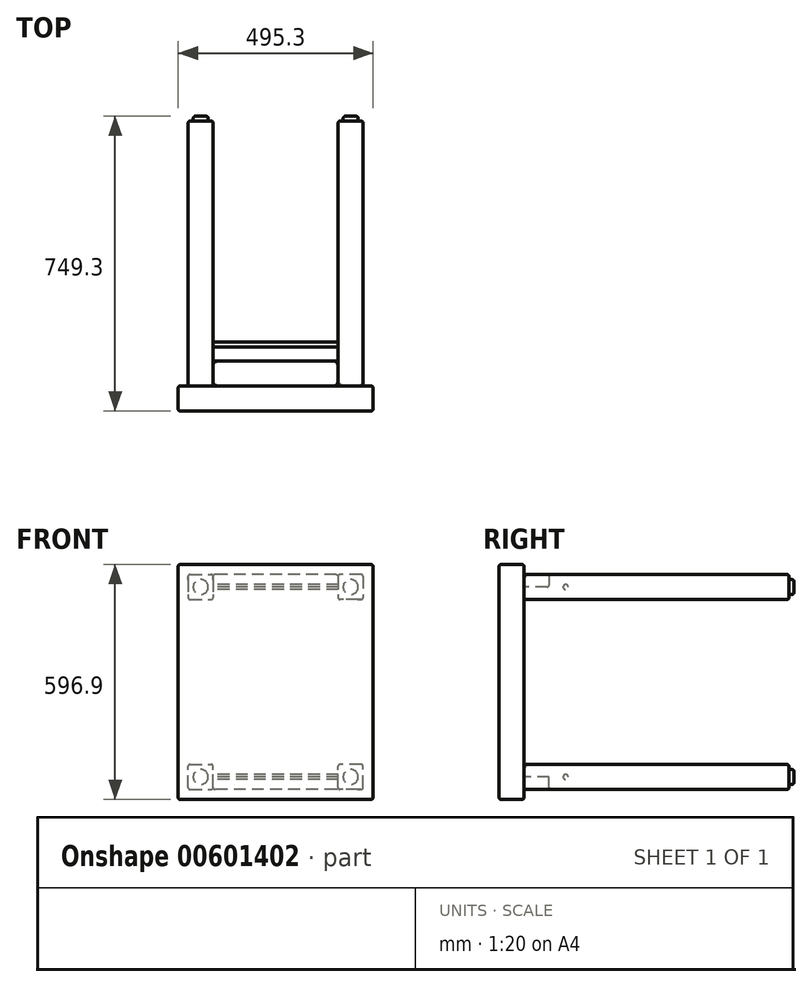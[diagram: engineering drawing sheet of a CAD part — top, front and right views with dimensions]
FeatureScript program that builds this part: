
annotation { "Feature Type Name" : "Feature", "Feature Type Description" : "" }
export const myFeature = defineFeature(function(context is Context, id is Id, definition is map)
    precondition{}
    {
        {
            var Q0;
            Q0=qCreatedBy(makeId("Front.planeOp"),FACE);
            var sketch = newSketch(context, id + "F0", { "sketchPlane" : qUnion([Q0])});
            skLineSegment(sketch, "E0.bottom", {"start": v(-247.65, 298.45) * mm, "end": v(247.65, 298.45) * mm});
            skLineSegment(sketch, "E0.top", {"start": v(-247.65, -298.45) * mm, "end": v(247.65, -298.45) * mm});
            skLineSegment(sketch, "E0.left", {"start": v(-247.65, 298.45) * mm, "end": v(-247.65, -298.45) * mm});
            skLineSegment(sketch, "E0.right", {"start": v(247.65, 298.45) * mm, "end": v(247.65, -298.45) * mm});
            skPoint(sketch, "E0.middle", {"position": v(0, 0) * mm});
            skSolve(sketch);
        }
        {
            var Q0;
            Q0 = qSketchRegion(id + "F0", true);
            extrude(context, id + "F1", {"entities" : qUnion([Q0]), "endBound" : BoundingType.SYMMETRIC, "depth" : 63.5 * mm, "offsetDistance" : 25.4 * mm});
        }
        {
            var Q0;
            Q0=makeQuery(id+"F1.opExtrude","CAP_FACE",FACE,{"disambiguationData":[OSD([sQuery(id+"F0.wireOp",EDGE,"E0.bottom"),sQuery(id+"F0.wireOp",EDGE,"E0.top"),sQuery(id+"F0.wireOp",EDGE,"E0.left"),sQuery(id+"F0.wireOp",EDGE,"E0.right")])],"isStart":true});
            var sketch = newSketch(context, id + "F2", { "sketchPlane" : qUnion([Q0])});
            skLineSegment(sketch, "E1.bottom", {"start": v(-222.25, 273.05) * mm, "end": v(222.25, 273.05) * mm, "construction": true});
            skLineSegment(sketch, "E1.top", {"start": v(-222.25, -273.05) * mm, "end": v(222.25, -273.05) * mm, "construction": true});
            skLineSegment(sketch, "E1.left", {"start": v(-222.25, 273.05) * mm, "end": v(-222.25, -273.05) * mm, "construction": true});
            skLineSegment(sketch, "E1.right", {"start": v(222.25, 273.05) * mm, "end": v(222.25, -273.05) * mm, "construction": true});
            skPoint(sketch, "E1.middle", {"position": v(0, 0) * mm});
            skLineSegment(sketch, "E2.bottom", {"start": v(-222.25, 273.05) * mm, "end": v(-158.75, 273.05) * mm});
            skLineSegment(sketch, "E2.top", {"start": v(-222.25, 209.55) * mm, "end": v(-158.75, 209.55) * mm});
            skLineSegment(sketch, "E2.left", {"start": v(-222.25, 273.05) * mm, "end": v(-222.25, 209.55) * mm});
            skLineSegment(sketch, "E2.right", {"start": v(-158.75, 273.05) * mm, "end": v(-158.75, 209.55) * mm});
            skLineSegment(sketch, "E3.bottom", {"start": v(222.25, 273.05) * mm, "end": v(158.75, 273.05) * mm});
            skLineSegment(sketch, "E3.top", {"start": v(222.25, 209.55) * mm, "end": v(158.75, 209.55) * mm});
            skLineSegment(sketch, "E3.left", {"start": v(222.25, 273.05) * mm, "end": v(222.25, 209.55) * mm});
            skLineSegment(sketch, "E3.right", {"start": v(158.75, 273.05) * mm, "end": v(158.75, 209.55) * mm});
            skLineSegment(sketch, "E4.bottom", {"start": v(222.25, -273.05) * mm, "end": v(158.75, -273.05) * mm});
            skLineSegment(sketch, "E4.top", {"start": v(222.25, -209.55) * mm, "end": v(158.75, -209.55) * mm});
            skLineSegment(sketch, "E4.left", {"start": v(222.25, -273.05) * mm, "end": v(222.25, -209.55) * mm});
            skLineSegment(sketch, "E4.right", {"start": v(158.75, -273.05) * mm, "end": v(158.75, -209.55) * mm});
            skLineSegment(sketch, "E5.bottom", {"start": v(-222.25, -273.05) * mm, "end": v(-158.75, -273.05) * mm});
            skLineSegment(sketch, "E5.top", {"start": v(-222.25, -209.55) * mm, "end": v(-158.75, -209.55) * mm});
            skLineSegment(sketch, "E5.left", {"start": v(-222.25, -273.05) * mm, "end": v(-222.25, -209.55) * mm});
            skLineSegment(sketch, "E5.right", {"start": v(-158.75, -273.05) * mm, "end": v(-158.75, -209.55) * mm});
            skLineSegment(sketch, "E6.bottom", {"start": v(-222.25, 209.55) * mm, "end": v(-190.5, 209.55) * mm});
            skLineSegment(sketch, "E6.top", {"start": v(-222.25, -209.55) * mm, "end": v(-190.5, -209.55) * mm});
            skLineSegment(sketch, "E6.left", {"start": v(-222.25, 209.55) * mm, "end": v(-222.25, -209.55) * mm});
            skLineSegment(sketch, "E6.right", {"start": v(-190.5, 209.55) * mm, "end": v(-190.5, -209.55) * mm});
            skLineSegment(sketch, "E7.bottom", {"start": v(222.25, -209.55) * mm, "end": v(190.5, -209.55) * mm});
            skLineSegment(sketch, "E7.top", {"start": v(222.25, 209.55) * mm, "end": v(190.5, 209.55) * mm});
            skLineSegment(sketch, "E7.left", {"start": v(222.25, -209.55) * mm, "end": v(222.25, 209.55) * mm});
            skLineSegment(sketch, "E7.right", {"start": v(190.5, -209.55) * mm, "end": v(190.5, 209.55) * mm});
            skLineSegment(sketch, "E8.bottom", {"start": v(-158.75, 273.05) * mm, "end": v(158.75, 273.05) * mm});
            skLineSegment(sketch, "E8.top", {"start": v(-158.75, 241.3) * mm, "end": v(158.75, 241.3) * mm});
            skLineSegment(sketch, "E8.left", {"start": v(-158.75, 273.05) * mm, "end": v(-158.75, 241.3) * mm});
            skLineSegment(sketch, "E8.right", {"start": v(158.75, 273.05) * mm, "end": v(158.75, 241.3) * mm});
            skLineSegment(sketch, "E9.bottom", {"start": v(-158.75, -273.05) * mm, "end": v(158.75, -273.05) * mm});
            skLineSegment(sketch, "E9.top", {"start": v(-158.75, -241.3) * mm, "end": v(158.75, -241.3) * mm});
            skLineSegment(sketch, "E9.left", {"start": v(-158.75, -273.05) * mm, "end": v(-158.75, -241.3) * mm});
            skLineSegment(sketch, "E9.right", {"start": v(158.75, -273.05) * mm, "end": v(158.75, -241.3) * mm});
            skSolve(sketch);
        }
        {
            var Q0;
            Q0=makeQuery(id+"F2.imprint","IMPRINT",FACE,{"disambiguationData":[TD([[makeQuery(id+"F2.imprint","IMPRINT",EDGE,{"derivedFrom":sQuery(id+"F2.wireOp",EDGE,"E3.bottom")}),1.0]])]});
            var Q1;
            Q1=makeQuery(id+"F2.imprint","IMPRINT",FACE,{"disambiguationData":[TD([[makeQuery(id+"F2.imprint","IMPRINT",EDGE,{"derivedFrom":sQuery(id+"F2.wireOp",EDGE,"E4.bottom")}),-1.0]])]});
            var Q2;
            Q2=makeQuery(id+"F2.imprint","IMPRINT",FACE,{"disambiguationData":[TD([[makeQuery(id+"F2.imprint","IMPRINT",EDGE,{"derivedFrom":sQuery(id+"F2.wireOp",EDGE,"E5.bottom")}),1.0]])]});
            var Q3;
            Q3=makeQuery(id+"F2.imprint","IMPRINT",FACE,{"disambiguationData":[TD([[makeQuery(id+"F2.imprint","IMPRINT",EDGE,{"derivedFrom":sQuery(id+"F2.wireOp",EDGE,"E2.bottom")}),-1.0]])]});
            extrude(context, id + "F3", {"entities" : qUnion([Q0, Q1, Q2, Q3]), "operationType" : NewBodyOperationType.ADD, "depth" : 673.1 * mm, "offsetDistance" : 25.4 * mm});
        }
        {
            var Q0;
            Q0=makeQuery(id+"F2.imprint","IMPRINT",FACE,{"disambiguationData":[TD([[makeQuery(id+"F2.imprint","IMPRINT",EDGE,{"derivedFrom":sQuery(id+"F2.wireOp",EDGE,"E8.bottom")}),-1.0]])]});
            var Q1;
            Q1=makeQuery(id+"F2.imprint","IMPRINT",FACE,{"disambiguationData":[TD([[makeQuery(id+"F2.imprint","IMPRINT",EDGE,{"derivedFrom":sQuery(id+"F2.wireOp",EDGE,"E7.bottom")}),-1.0]])]});
            var Q2;
            Q2=makeQuery(id+"F2.imprint","IMPRINT",FACE,{"disambiguationData":[TD([[makeQuery(id+"F2.imprint","IMPRINT",EDGE,{"derivedFrom":sQuery(id+"F2.wireOp",EDGE,"E9.bottom")}),1.0]])]});
            var Q3;
            Q3=makeQuery(id+"F2.imprint","IMPRINT",FACE,{"disambiguationData":[TD([[makeQuery(id+"F2.imprint","IMPRINT",EDGE,{"derivedFrom":sQuery(id+"F2.wireOp",EDGE,"E6.bottom")}),-1.0]])]});
            extrude(context, id + "F4", {"entities" : qUnion([Q0, Q1, Q2, Q3]), "depth" : 63.5 * mm, "offsetDistance" : 25.4 * mm});
        }
        {
            var Q0;
            Q0=makeQuery(id+"F3.opExtrude","CAP_FACE",FACE,{"disambiguationData":[OSD([sQuery(id+"F2.wireOp",EDGE,"E3.bottom"),sQuery(id+"F2.wireOp",EDGE,"E3.top"),sQuery(id+"F2.wireOp",EDGE,"E3.left"),sQuery(id+"F2.wireOp",EDGE,"E3.right"),sQuery(id+"F2.wireOp",EDGE,"E7.top"),sQuery(id+"F2.wireOp",EDGE,"E8.right")])],"isStart":false});
            var sketch = newSketch(context, id + "F5", { "sketchPlane" : qUnion([Q0])});
            skCircle(sketch, "E10", {"center": v(-190.5, 241.3) * mm, "radius": 19.05 * mm});
            skPoint(sketch, "E10.centerSnap0", {"position": v(-190.5, 209.55) * mm});
            skPoint(sketch, "E10.centerSnap1", {"position": v(-222.25, 241.3) * mm});
            skCircle(sketch, "E11", {"center": v(-190.5, -241.3) * mm, "radius": 19.05 * mm});
            skPoint(sketch, "E11.centerSnap0", {"position": v(-222.25, -241.3) * mm});
            skPoint(sketch, "E11.centerSnap1", {"position": v(-190.5, -273.05) * mm});
            skCircle(sketch, "E12", {"center": v(190.5, -241.3) * mm, "radius": 19.05 * mm});
            skPoint(sketch, "E12.centerSnap0", {"position": v(190.5, -273.05) * mm});
            skPoint(sketch, "E12.centerSnap1", {"position": v(222.25, -241.3) * mm});
            skCircle(sketch, "E13", {"center": v(190.5, 241.3) * mm, "radius": 19.05 * mm});
            skPoint(sketch, "E13.centerSnap0", {"position": v(158.75, 241.3) * mm});
            skPoint(sketch, "E13.centerSnap1", {"position": v(190.5, 209.55) * mm});
            skSolve(sketch);
        }
        {
            var Q0;
            Q0=makeQuery(id+"F5.imprint","IMPRINT",FACE,{"disambiguationData":[TD([[makeQuery(id+"F5.imprint","IMPRINT",EDGE,{"derivedFrom":sQuery(id+"F5.wireOp",EDGE,"E10")}),1.0]])]});
            var Q1;
            Q1=makeQuery(id+"F5.imprint","IMPRINT",FACE,{"disambiguationData":[TD([[makeQuery(id+"F5.imprint","IMPRINT",EDGE,{"derivedFrom":sQuery(id+"F5.wireOp",EDGE,"E11")}),1.0]])]});
            var Q2;
            Q2=makeQuery(id+"F5.imprint","IMPRINT",FACE,{"disambiguationData":[TD([[makeQuery(id+"F5.imprint","IMPRINT",EDGE,{"derivedFrom":sQuery(id+"F5.wireOp",EDGE,"E12")}),1.0]])]});
            var Q3;
            Q3=makeQuery(id+"F5.imprint","IMPRINT",FACE,{"disambiguationData":[TD([[makeQuery(id+"F5.imprint","IMPRINT",EDGE,{"derivedFrom":sQuery(id+"F5.wireOp",EDGE,"E13")}),1.0]])]});
            extrude(context, id + "F6", {"entities" : qUnion([Q0, Q1, Q2, Q3]), "depth" : 12.7 * mm, "offsetDistance" : 25.4 * mm});
        }
        {
            var Q0;
            Q0=makeQuery(id+"F6.opExtrude","CAP_FACE",FACE,{"disambiguationData":[OSD([sQuery(id+"F5.wireOp",EDGE,"E10")])],"isStart":false});
            var Q1;
            Q1=makeQuery(id+"F6.opExtrude","CAP_FACE",FACE,{"disambiguationData":[OSD([sQuery(id+"F5.wireOp",EDGE,"E13")])],"isStart":false});
            var Q2;
            Q2=makeQuery(id+"F6.opExtrude","CAP_FACE",FACE,{"disambiguationData":[OSD([sQuery(id+"F5.wireOp",EDGE,"E12")])],"isStart":false});
            var Q3;
            Q3=makeQuery(id+"F6.opExtrude","CAP_FACE",FACE,{"disambiguationData":[OSD([sQuery(id+"F5.wireOp",EDGE,"E11")])],"isStart":false});
            fillet(context, id + "F7", {"entities" : qUnion([Q0, Q1, Q2, Q3]), "radius" : 6.35 * mm, "tangentPropagation" : true, "allowEdgeOverflow" : false});
        }
        {
            var Q0;
            Q0=makeQuery(id+"F4.opExtrude","CAP_EDGE",EDGE,{"disambiguationData":[OSD([sQuery(id+"F2.wireOp",EDGE,"E8.bottom")])],"isStart":false});
            var Q1;
            Q1=makeQuery(id+"F4.opExtrude","CAP_EDGE",EDGE,{"disambiguationData":[OSD([sQuery(id+"F2.wireOp",EDGE,"E8.top")])],"isStart":false});
            var Q2;
            Q2=makeQuery(id+"F4.opExtrude","SWEPT_FACE",FACE,{"disambiguationData":[OSD([sQuery(id+"F2.wireOp",EDGE,"E8.bottom")])]});
            var Q3;
            Q3=makeQuery(id+"F3.opExtrude","SWEPT_FACE",FACE,{"disambiguationData":[OSD([sQuery(id+"F2.wireOp",EDGE,"E3.bottom")])]});
            var Q4;
            Q4=makeQuery(id+"F3.opExtrude","SWEPT_FACE",FACE,{"disambiguationData":[OSD([sQuery(id+"F2.wireOp",EDGE,"E4.top"),sQuery(id+"F2.wireOp",EDGE,"E7.bottom")])]});
            var Q5;
            Q5=makeQuery(id+"F3.opExtrude","SWEPT_FACE",FACE,{"disambiguationData":[OSD([sQuery(id+"F2.wireOp",EDGE,"E5.top"),sQuery(id+"F2.wireOp",EDGE,"E6.top")])]});
            var Q6;
            Q6=makeQuery(id+"F3.opExtrude","SWEPT_FACE",FACE,{"disambiguationData":[OSD([sQuery(id+"F2.wireOp",EDGE,"E2.bottom")])]});
            var Q7;
            Q7=makeQuery(id+"F3.opExtrude","SWEPT_EDGE",EDGE,{"disambiguationData":[OSD([sQuery(id+"F2.wireOp",EDGE,"E3.left"),sQuery(id+"F2.wireOp",EDGE,"E7.top"),sQuery(id+"F2.wireOp",EDGE,"E7.left")])]});
            var Q8;
            Q8=makeQuery(id+"F3.opExtrude","SWEPT_EDGE",EDGE,{"disambiguationData":[OSD([sQuery(id+"F2.wireOp",EDGE,"E4.bottom"),sQuery(id+"F2.wireOp",EDGE,"E4.left")])]});
            var Q9;
            Q9=makeQuery(id+"F1.opExtrude","CAP_EDGE",EDGE,{"disambiguationData":[OSD([sQuery(id+"F0.wireOp",EDGE,"E0.left")])],"isStart":true});
            var Q10;
            Q10=makeQuery(id+"F4.opExtrude","SWEPT_FACE",FACE,{"disambiguationData":[OSD([sQuery(id+"F2.wireOp",EDGE,"E7.left")])]});
            var Q11;
            Q11=makeQuery(id+"F1.opExtrude","SWEPT_FACE",FACE,{"disambiguationData":[OSD([sQuery(id+"F0.wireOp",EDGE,"E0.left")])]});
            var Q12;
            Q12=makeQuery(id+"F1.opExtrude","CAP_FACE",FACE,{"disambiguationData":[OSD([sQuery(id+"F0.wireOp",EDGE,"E0.bottom"),sQuery(id+"F0.wireOp",EDGE,"E0.top"),sQuery(id+"F0.wireOp",EDGE,"E0.left"),sQuery(id+"F0.wireOp",EDGE,"E0.right")])],"isStart":false});
            var Q13;
            Q13=makeQuery(id+"F3.opExtrude","SWEPT_FACE",FACE,{"disambiguationData":[OSD([sQuery(id+"F2.wireOp",EDGE,"E2.left")])]});
            var Q14;
            Q14=makeQuery(id+"F3.opExtrude","SWEPT_FACE",FACE,{"disambiguationData":[OSD([sQuery(id+"F2.wireOp",EDGE,"E5.left")])]});
            var Q15;
            Q15=makeQuery(id+"F3.opExtrude","SWEPT_EDGE",EDGE,{"disambiguationData":[OSD([sQuery(id+"F2.wireOp",EDGE,"E4.bottom"),sQuery(id+"F2.wireOp",EDGE,"E9.bottom"),sQuery(id+"F2.wireOp",EDGE,"E9.right")])]});
            var Q16;
            Q16=makeQuery(id+"F4.opExtrude","SWEPT_FACE",FACE,{"disambiguationData":[OSD([sQuery(id+"F2.wireOp",EDGE,"E6.left")])]});
            var Q17;
            Q17=makeQuery(id+"F4.opExtrude","SWEPT_FACE",FACE,{"disambiguationData":[OSD([sQuery(id+"F2.wireOp",EDGE,"E9.bottom")])]});
            var Q18;
            Q18=makeQuery(id+"F1.opExtrude","SWEPT_EDGE",EDGE,{"disambiguationData":[OSD([sQuery(id+"F0.wireOp",EDGE,"E0.top"),sQuery(id+"F0.wireOp",EDGE,"E0.right")])]});
            var Q19;
            Q19=makeQuery(id+"F1.opExtrude","SWEPT_FACE",FACE,{"disambiguationData":[OSD([sQuery(id+"F0.wireOp",EDGE,"E0.bottom")])]});
            var Q20;
            Q20=makeQuery(id+"F1.opExtrude","SWEPT_FACE",FACE,{"disambiguationData":[OSD([sQuery(id+"F0.wireOp",EDGE,"E0.right")])]});
            var Q21;
            Q21=makeQuery(id+"F1.opExtrude","SWEPT_FACE",FACE,{"disambiguationData":[OSD([sQuery(id+"F0.wireOp",EDGE,"E0.top")])]});
            var Q22;
            Q22=makeQuery(id+"F3.opExtrude","CAP_FACE",FACE,{"disambiguationData":[OSD([sQuery(id+"F2.wireOp",EDGE,"E4.bottom"),sQuery(id+"F2.wireOp",EDGE,"E4.top"),sQuery(id+"F2.wireOp",EDGE,"E4.left"),sQuery(id+"F2.wireOp",EDGE,"E4.right"),sQuery(id+"F2.wireOp",EDGE,"E7.bottom"),sQuery(id+"F2.wireOp",EDGE,"E9.right")])],"isStart":false});
            var Q23;
            Q23=makeQuery(id+"F3.opExtrude","CAP_FACE",FACE,{"disambiguationData":[OSD([sQuery(id+"F2.wireOp",EDGE,"E5.bottom"),sQuery(id+"F2.wireOp",EDGE,"E5.top"),sQuery(id+"F2.wireOp",EDGE,"E5.left"),sQuery(id+"F2.wireOp",EDGE,"E5.right"),sQuery(id+"F2.wireOp",EDGE,"E6.top"),sQuery(id+"F2.wireOp",EDGE,"E9.left")])],"isStart":false});
            var Q24;
            Q24=makeQuery(id+"F3.opExtrude","CAP_FACE",FACE,{"disambiguationData":[OSD([sQuery(id+"F2.wireOp",EDGE,"E2.bottom"),sQuery(id+"F2.wireOp",EDGE,"E2.top"),sQuery(id+"F2.wireOp",EDGE,"E2.left"),sQuery(id+"F2.wireOp",EDGE,"E2.right"),sQuery(id+"F2.wireOp",EDGE,"E6.bottom"),sQuery(id+"F2.wireOp",EDGE,"E8.left")])],"isStart":false});
            var Q25;
            Q25=makeQuery(id+"F3.opExtrude","SWEPT_FACE",FACE,{"disambiguationData":[OSD([sQuery(id+"F2.wireOp",EDGE,"E2.right"),sQuery(id+"F2.wireOp",EDGE,"E8.left")])]});
            var Q26;
            Q26=makeQuery(id+"F3.opExtrude","CAP_FACE",FACE,{"disambiguationData":[OSD([sQuery(id+"F2.wireOp",EDGE,"E3.bottom"),sQuery(id+"F2.wireOp",EDGE,"E3.top"),sQuery(id+"F2.wireOp",EDGE,"E3.left"),sQuery(id+"F2.wireOp",EDGE,"E3.right"),sQuery(id+"F2.wireOp",EDGE,"E7.top"),sQuery(id+"F2.wireOp",EDGE,"E8.right")])],"isStart":false});
            var Q27;
            Q27=makeQuery(id+"F3.opExtrude","SWEPT_EDGE",EDGE,{"disambiguationData":[OSD([sQuery(id+"F2.wireOp",EDGE,"E3.top"),sQuery(id+"F2.wireOp",EDGE,"E3.right")])]});
            var Q28;
            Q28=makeQuery(id+"F3.opExtrude","SWEPT_EDGE",EDGE,{"disambiguationData":[OSD([sQuery(id+"F2.wireOp",EDGE,"E5.bottom"),sQuery(id+"F2.wireOp",EDGE,"E9.bottom"),sQuery(id+"F2.wireOp",EDGE,"E9.left")])]});
            fillet(context, id + "F8", {"entities" : qUnion([Q0, Q1, Q2, Q3, Q4, Q5, Q6, Q7, Q8, Q9, Q10, Q11, Q12, Q13, Q14, Q15, Q16, Q17, Q18, Q19, Q20, Q21, Q22, Q23, Q24, Q25, Q26, Q27, Q28]), "radius" : 5.08 * mm, "tangentPropagation" : true, "allowEdgeOverflow" : false});
        }
        {
            var Q0;
            Q0=makeQuery(id+"F3.opExtrude","SWEPT_FACE",FACE,{"disambiguationData":[OSD([sQuery(id+"F2.wireOp",EDGE,"E4.right"),sQuery(id+"F2.wireOp",EDGE,"E9.right")])]});
            var sketch = newSketch(context, id + "F9", { "sketchPlane" : qUnion([Q0])});
            skCircle(sketch, "E14", {"center": v(137.5, -241.3) * mm, "radius": 6.45 * mm});
            skSolve(sketch);
        }
        {
            var Q0;
            Q0 = qSketchRegion(id + "F9", true);
            extrude(context, id + "F10", {"entities" : qUnion([Q0]), "depth" : 317.5 * mm, "offsetDistance" : 25.4 * mm});
        }
        {
            var Q0;
            Q0=makeQuery(id+"F1.opExtrude","SWEPT_FACE",FACE,{"disambiguationData":[OSD([sQuery(id+"F0.wireOp",EDGE,"E0.top")])]});
            var Q1;
            Q1=makeQuery(id+"F1.opExtrude","SWEPT_FACE",FACE,{"disambiguationData":[OSD([sQuery(id+"F0.wireOp",EDGE,"E0.bottom")])]});
            cPlane(context, id + "F11", {"entities" : qUnion([Q0, Q1]), "cplaneType" : CPlaneType.MID_PLANE, "offset" : 25.4 * mm, "width" : 152.4 * mm, "height" : 152.4 * mm});
        }
        {
            var Q0;
            Q0=makeQuery(id+"F10.opExtrude","SWEPT_BODY",BODY,{"disambiguationData":[OSD([sQuery(id+"F9.wireOp",EDGE,"E14")])]});
            var Q1;
            Q1=qCreatedBy(id+"F11.planeOp",FACE);
            mirror(context, id + "F12", {"entities" : qUnion([Q0]), "mirrorPlane" : qUnion([Q1])});
        }
    });
